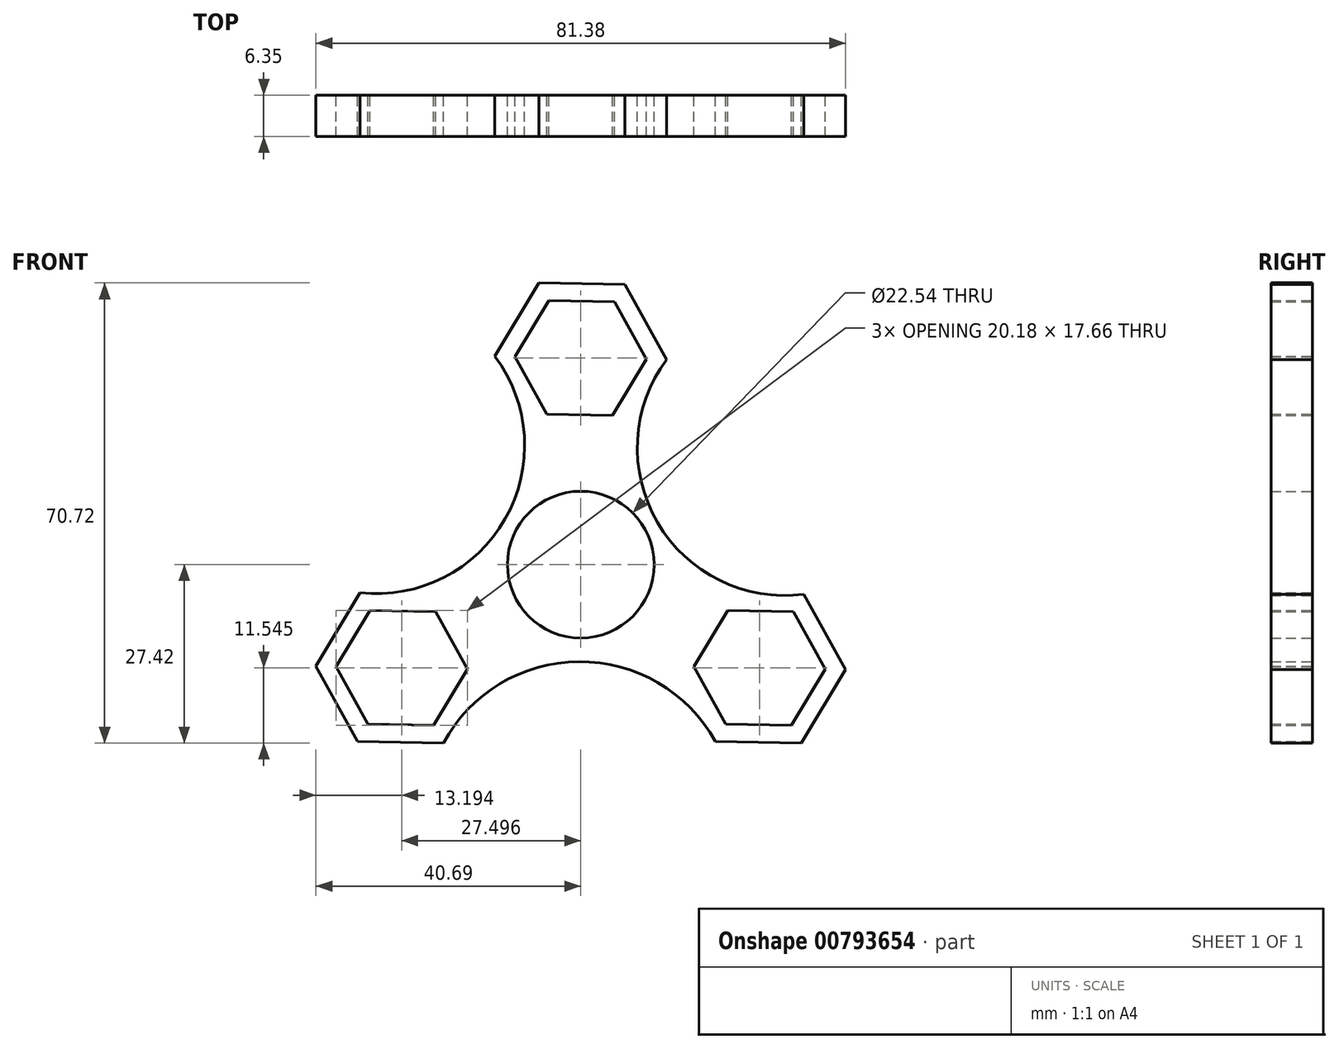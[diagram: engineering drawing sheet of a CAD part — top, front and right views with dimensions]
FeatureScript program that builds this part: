
annotation { "Feature Type Name" : "Feature", "Feature Type Description" : "" }
export const myFeature = defineFeature(function(context is Context, id is Id, definition is map)
    precondition{}
    {
        {
            var Q0;
            Q0=qCreatedBy(makeId("Front.planeOp"),FACE);
            var sketch = newSketch(context, id + "F0", { "sketchPlane" : qUnion([Q0])});
            skCircle(sketch, "E0", {"center": v(0, 0) * mm, "radius": 7.97 * mm});
            skCircle(sketch, "E1", {"center": v(0, 0) * mm, "radius": 11.27 * mm});
            skCircle(sketch, "E2.cCircle", {"center": v(0, 31.75) * mm, "radius": 11.43 * mm, "construction": true});
            skLineSegment(sketch, "E2.0", {"start": v(-13.2, 31.99) * mm, "end": v(-6.4, 43.3) * mm});
            skLineSegment(sketch, "E2.1", {"start": v(-6.4, 43.3) * mm, "end": v(6.8, 43.06) * mm});
            skLineSegment(sketch, "E2.2", {"start": v(6.8, 43.06) * mm, "end": v(13.2, 31.51) * mm});
            skLineSegment(sketch, "E2.3", {"start": v(13.2, 31.51) * mm, "end": v(6.4, 20.2) * mm});
            skLineSegment(sketch, "E2.4", {"start": v(6.4, 20.2) * mm, "end": v(-6.8, 20.44) * mm});
            skLineSegment(sketch, "E2.5", {"start": v(-6.8, 20.44) * mm, "end": v(-13.2, 31.99) * mm});
            skPoint(sketch, "E2.0.midPoint", {"position": v(-9.8, 37.64) * mm});
            skCircle(sketch, "E3.cCircle", {"center": v(0, 31.75) * mm, "radius": 8.74 * mm, "construction": true});
            skLineSegment(sketch, "E3.0", {"start": v(-10.09, 31.93) * mm, "end": v(-4.89, 40.58) * mm});
            skLineSegment(sketch, "E3.1", {"start": v(-4.89, 40.58) * mm, "end": v(5.2, 40.4) * mm});
            skLineSegment(sketch, "E3.2", {"start": v(5.2, 40.4) * mm, "end": v(10.09, 31.57) * mm});
            skLineSegment(sketch, "E3.3", {"start": v(10.09, 31.57) * mm, "end": v(4.89, 22.92) * mm});
            skLineSegment(sketch, "E3.4", {"start": v(4.89, 22.92) * mm, "end": v(-5.2, 23.1) * mm});
            skLineSegment(sketch, "E3.5", {"start": v(-5.2, 23.1) * mm, "end": v(-10.09, 31.93) * mm});
            skPoint(sketch, "E3.0.midPoint", {"position": v(-7.49, 36.26) * mm});
            skLineSegment(sketch, "E4.1.0", {"start": v(-22.61, -24.7) * mm, "end": v(-32.7, -24.52) * mm});
            skCircle(sketch, "E4.1.1", {"center": v(-27.5, -15.87) * mm, "radius": 8.74 * mm, "construction": true});
            skLineSegment(sketch, "E4.1.2", {"start": v(-32.7, -24.52) * mm, "end": v(-37.58, -15.7) * mm});
            skLineSegment(sketch, "E4.1.3", {"start": v(-37.58, -15.7) * mm, "end": v(-32.38, -7.05) * mm});
            skLineSegment(sketch, "E4.1.4", {"start": v(-32.38, -7.05) * mm, "end": v(-22.3, -7.23) * mm});
            skLineSegment(sketch, "E4.1.5", {"start": v(-22.3, -7.23) * mm, "end": v(-17.4, -16.06) * mm});
            skLineSegment(sketch, "E4.1.6", {"start": v(-17.4, -16.06) * mm, "end": v(-22.61, -24.7) * mm});
            skCircle(sketch, "E4.1.7", {"center": v(-27.5, -15.87) * mm, "radius": 11.43 * mm, "construction": true});
            skLineSegment(sketch, "E4.1.8", {"start": v(-14.3, -16.11) * mm, "end": v(-21.1, -27.42) * mm});
            skLineSegment(sketch, "E4.1.9", {"start": v(-21.1, -27.42) * mm, "end": v(-34.3, -27.18) * mm});
            skLineSegment(sketch, "E4.1.10", {"start": v(-34.3, -27.18) * mm, "end": v(-40.7, -15.64) * mm});
            skLineSegment(sketch, "E4.1.11", {"start": v(-40.7, -15.64) * mm, "end": v(-33.89, -4.33) * mm});
            skLineSegment(sketch, "E4.1.12", {"start": v(-33.89, -4.33) * mm, "end": v(-20.7, -4.57) * mm});
            skLineSegment(sketch, "E4.1.13", {"start": v(-20.7, -4.57) * mm, "end": v(-14.3, -16.11) * mm});
            skLineSegment(sketch, "E4.2.0", {"start": v(32.7, -7.23) * mm, "end": v(37.58, -16.06) * mm});
            skCircle(sketch, "E4.2.1", {"center": v(27.5, -15.88) * mm, "radius": 8.74 * mm, "construction": true});
            skLineSegment(sketch, "E4.2.2", {"start": v(37.58, -16.06) * mm, "end": v(32.38, -24.7) * mm});
            skLineSegment(sketch, "E4.2.3", {"start": v(32.38, -24.7) * mm, "end": v(22.3, -24.52) * mm});
            skLineSegment(sketch, "E4.2.4", {"start": v(22.3, -24.52) * mm, "end": v(17.4, -15.7) * mm});
            skLineSegment(sketch, "E4.2.5", {"start": v(17.4, -15.7) * mm, "end": v(22.61, -7.05) * mm});
            skLineSegment(sketch, "E4.2.6", {"start": v(22.61, -7.05) * mm, "end": v(32.7, -7.23) * mm});
            skCircle(sketch, "E4.2.7", {"center": v(27.5, -15.88) * mm, "radius": 11.43 * mm, "construction": true});
            skLineSegment(sketch, "E4.2.8", {"start": v(21.1, -4.33) * mm, "end": v(34.3, -4.57) * mm});
            skLineSegment(sketch, "E4.2.9", {"start": v(34.3, -4.57) * mm, "end": v(40.7, -16.11) * mm});
            skLineSegment(sketch, "E4.2.10", {"start": v(40.7, -16.11) * mm, "end": v(33.89, -27.42) * mm});
            skLineSegment(sketch, "E4.2.11", {"start": v(33.89, -27.42) * mm, "end": v(20.7, -27.18) * mm});
            skLineSegment(sketch, "E4.2.12", {"start": v(20.7, -27.18) * mm, "end": v(14.3, -15.64) * mm});
            skLineSegment(sketch, "E4.2.13", {"start": v(14.3, -15.64) * mm, "end": v(21.1, -4.33) * mm});
            skArc(sketch, "E5", {"start": v(-33.89, -4.33) * mm, "mid": v(-11.6, 7.03) * mm, "end": v(-13.2, 31.99) * mm});
            skArc(sketch, "E6", {"start": v(20.7, -27.18) * mm, "mid": v(-0.28, -14.9) * mm, "end": v(-21.1, -27.42) * mm});
            skArc(sketch, "E7", {"start": v(13.2, 31.51) * mm, "mid": v(11.8, 6.48) * mm, "end": v(34.3, -4.57) * mm});
            skSolve(sketch);
        }
        {
            var Q0;
            {var subQ4=sQuery(id+"F0.wireOp",EDGE,"E2.0");Q0=makeQuery(id+"F0.imprint","IMPRINT",FACE,{"disambiguationData":[TD([[makeQuery(id+"F0.imprint","IMPRINT",EDGE,{"derivedFrom":subQ4}),-1.0]])]});}
            var Q1;
            Q1=makeQuery(id+"F0.imprint","IMPRINT",FACE,{"disambiguationData":[TD([[makeQuery(id+"F0.imprint","IMPRINT",EDGE,{"derivedFrom":sQuery(id+"F0.wireOp",EDGE,"E1")}),-1.0]])]});
            var Q2;
            Q2=makeQuery(id+"F0.imprint","IMPRINT",FACE,{"disambiguationData":[TD([[makeQuery(id+"F0.imprint","IMPRINT",EDGE,{"derivedFrom":sQuery(id+"F0.wireOp",EDGE,"E4.1.0")}),1.0]])]});
            var Q3;
            Q3=makeQuery(id+"F0.imprint","IMPRINT",FACE,{"disambiguationData":[TD([[makeQuery(id+"F0.imprint","IMPRINT",EDGE,{"derivedFrom":sQuery(id+"F0.wireOp",EDGE,"E4.2.0")}),1.0]])]});
            extrude(context, id + "F1", {"entities" : qUnion([Q0, Q1, Q2, Q3]), "depth" : 6.35 * mm, "offsetDistance" : 25.4 * mm});
        }
    });
